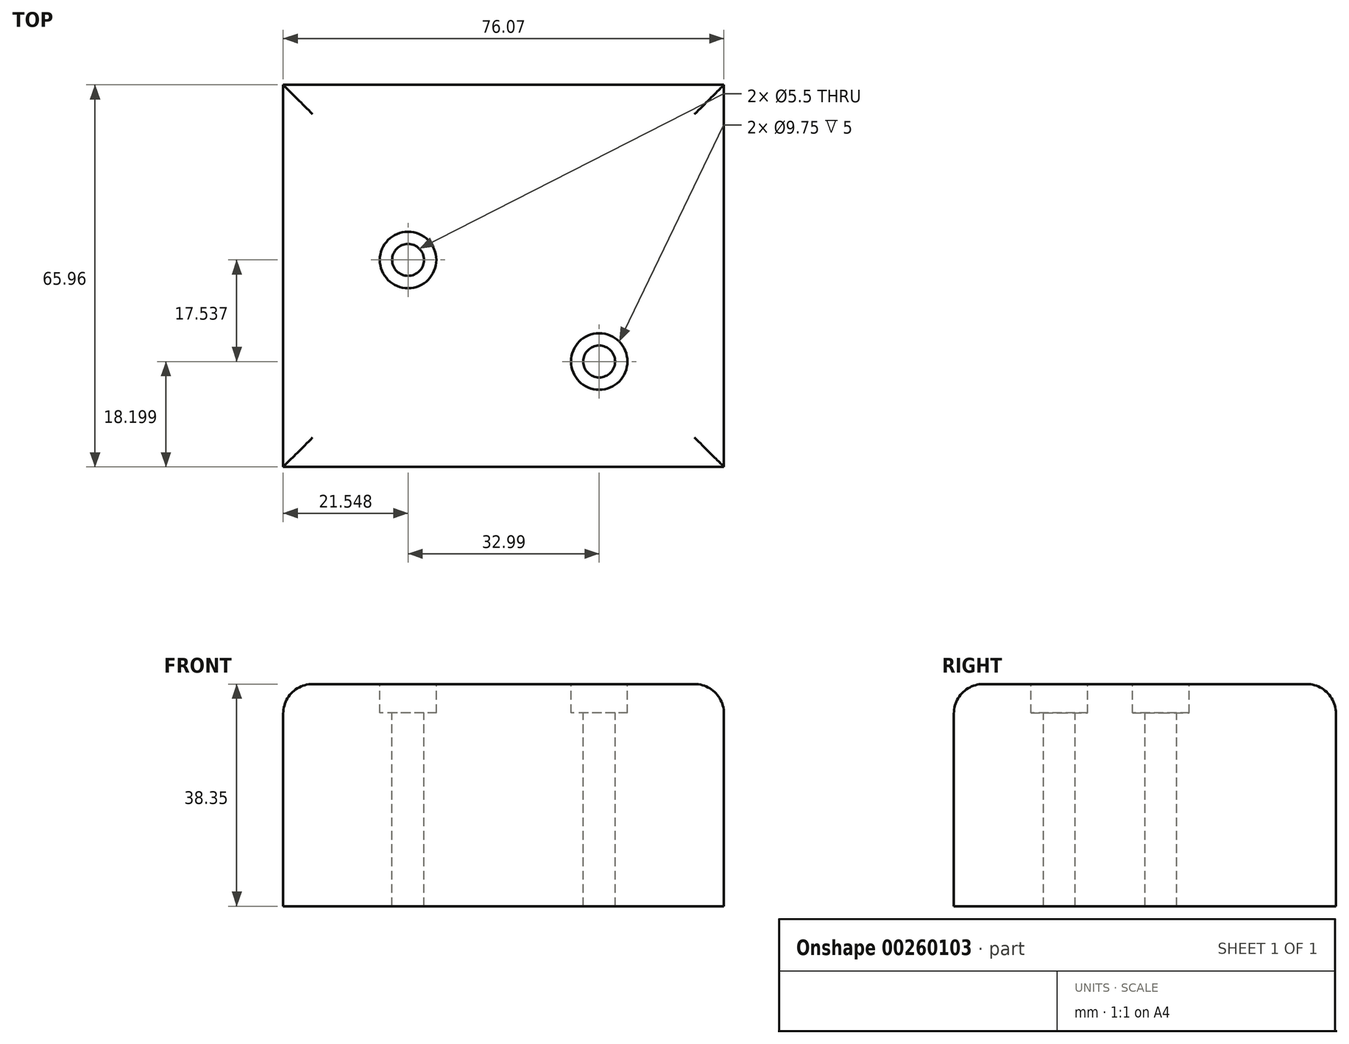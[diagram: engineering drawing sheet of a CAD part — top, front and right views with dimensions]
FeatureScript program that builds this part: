
annotation { "Feature Type Name" : "Feature", "Feature Type Description" : "" }
export const myFeature = defineFeature(function(context is Context, id is Id, definition is map)
    precondition{}
    {
        {
            var Q0;
            Q0=qCreatedBy(makeId("Top.planeOp"),FACE);
            var sketch = newSketch(context, id + "F0", { "sketchPlane" : qUnion([Q0])});
            skLineSegment(sketch, "E0.bottom", {"start": v(-35.06, 36.05) * mm, "end": v(41, 36.05) * mm});
            skLineSegment(sketch, "E0.top", {"start": v(-35.06, -29.9) * mm, "end": v(41, -29.9) * mm});
            skLineSegment(sketch, "E0.left", {"start": v(-35.06, 36.05) * mm, "end": v(-35.06, -29.9) * mm});
            skLineSegment(sketch, "E0.right", {"start": v(41, 36.05) * mm, "end": v(41, -29.9) * mm});
            skSolve(sketch);
        }
        {
            var Q0;
            Q0 = qSketchRegion(id + "F0", true);
            extrude(context, id + "F1", {"entities" : qUnion([Q0]), "depth" : 38.35 * mm});
        }
        {
            var Q0;
            Q0=makeQuery(id+"F1.opExtrude","CAP_EDGE",EDGE,{"disambiguationData":[OSD([sQuery(id+"F0.wireOp",EDGE,"E0.top")])],"isStart":false});
            var Q1;
            Q1=makeQuery(id+"F1.opExtrude","CAP_EDGE",EDGE,{"disambiguationData":[OSD([sQuery(id+"F0.wireOp",EDGE,"E0.right")])],"isStart":false});
            var Q2;
            Q2=makeQuery(id+"F1.opExtrude","CAP_EDGE",EDGE,{"disambiguationData":[OSD([sQuery(id+"F0.wireOp",EDGE,"E0.bottom")])],"isStart":false});
            var Q3;
            Q3=makeQuery(id+"F1.opExtrude","CAP_EDGE",EDGE,{"disambiguationData":[OSD([sQuery(id+"F0.wireOp",EDGE,"E0.left")])],"isStart":false});
            fillet(context, id + "F2", {"entities" : qUnion([Q0, Q1, Q2, Q3]), "radius" : 5.08 * mm, "tangentPropagation" : true, "allowEdgeOverflow" : false});
        }
        {
            var Q0;
            Q0=makeQuery(id+"F1.opExtrude","CAP_FACE",FACE,{"disambiguationData":[OSD([sQuery(id+"F0.wireOp",EDGE,"E0.bottom"),sQuery(id+"F0.wireOp",EDGE,"E0.top"),sQuery(id+"F0.wireOp",EDGE,"E0.left"),sQuery(id+"F0.wireOp",EDGE,"E0.right")])],"isStart":false});
            var sketch = newSketch(context, id + "F3", { "sketchPlane" : qUnion([Q0])});
            skPoint(sketch, "E1", {"position": v(-13.51, 5.83) * mm});
            skPoint(sketch, "E2", {"position": v(19.48, -11.71) * mm});
            skSolve(sketch);
        }
        {
            var Q0;
            Q0=sQuery(id+"F3.wireOp",VERTEX,"E1");
            var Q1;
            Q1=sQuery(id+"F3.wireOp",VERTEX,"E2");
            var Q2;
            Q2=makeQuery(id+"F1.opExtrude","SWEPT_BODY",BODY,{"disambiguationData":[OSD([sQuery(id+"F0.wireOp",EDGE,"E0.bottom"),sQuery(id+"F0.wireOp",EDGE,"E0.top"),sQuery(id+"F0.wireOp",EDGE,"E0.left"),sQuery(id+"F0.wireOp",EDGE,"E0.right")])]});
            hole(context, id + "F4", {"style" : HoleStyle.C_BORE, "endStyle" : HoleEndStyle.THROUGH, "standardTappedOrClearance" : lookupTablePath({ "standard" : "ISO", "fit" : "Normal", "size" : "M5", "type" : "Clearance" }), "standardBlindInLast" : lookupTablePath({ "fit" : "Standard", "standard" : "ISO", "size" : "M5", "type" : "Clearance" }), "holeDiameter" : 5.5 * mm, "cBoreDiameter" : 9.75 * mm, "cBoreDepth" : 5 * mm, "tappedDepth" : 12.7 * mm, "tapClearance" : 3, "locations" : qUnion([Q0, Q1]), "scope" : qUnion([Q2])});
        }
    });
